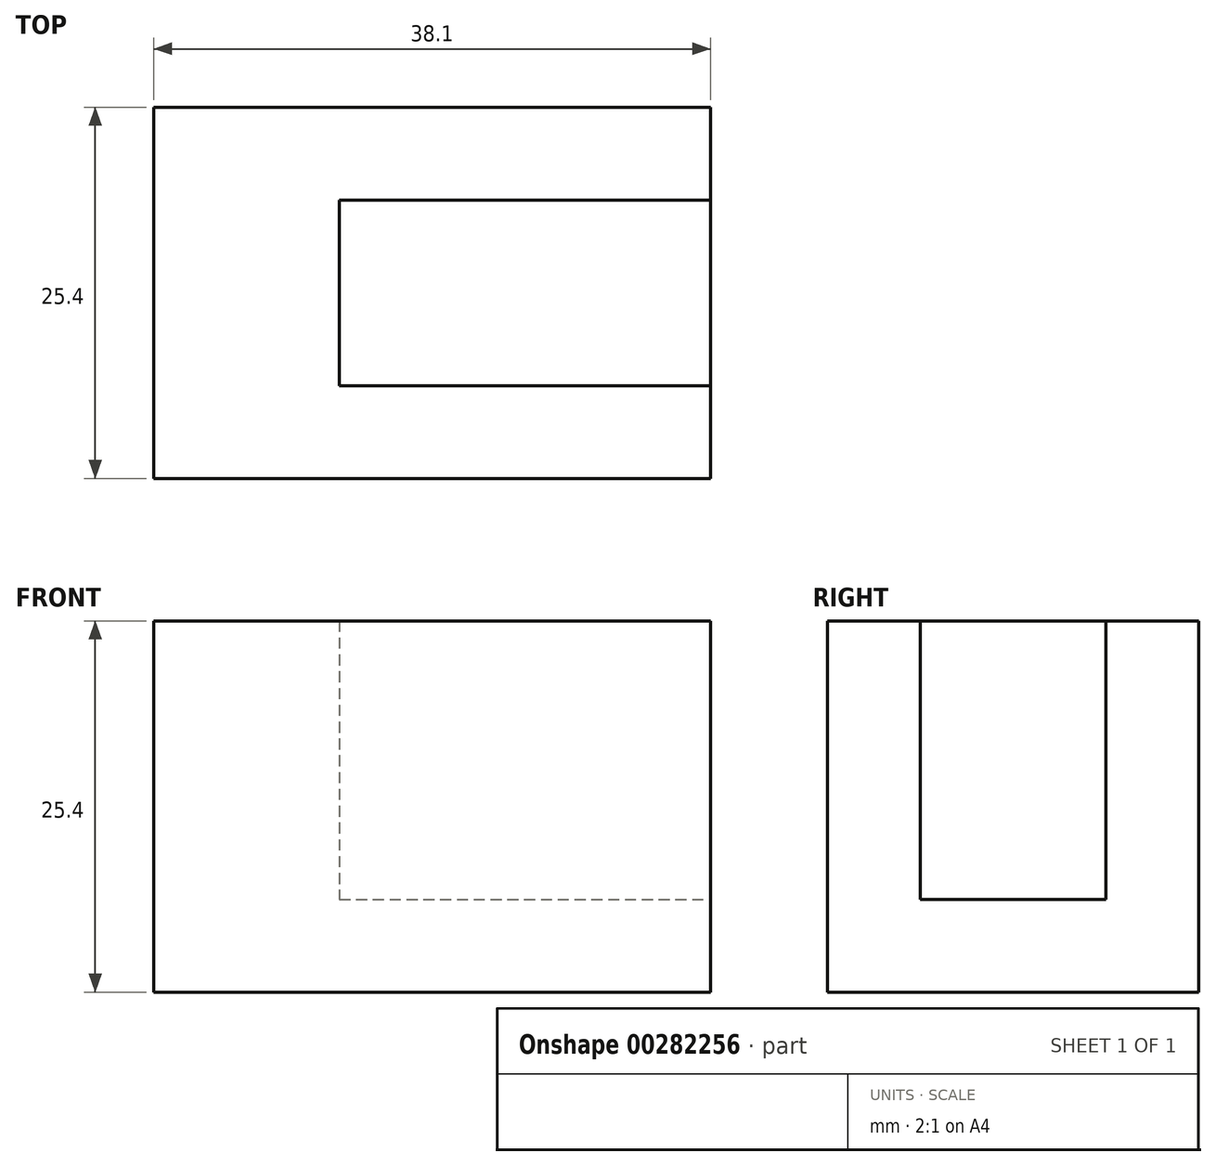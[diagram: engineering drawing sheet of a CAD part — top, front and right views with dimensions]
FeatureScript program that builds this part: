
annotation { "Feature Type Name" : "Feature", "Feature Type Description" : "" }
export const myFeature = defineFeature(function(context is Context, id is Id, definition is map)
    precondition{}
    {
        {
            var Q0;
            Q0=qCreatedBy(makeId("Front.planeOp"),FACE);
            var sketch = newSketch(context, id + "F0", { "sketchPlane" : qUnion([Q0])});
            skLineSegment(sketch, "E0", {"start": v(0, 0) * mm, "end": v(-38.1, 0) * mm});
            skLineSegment(sketch, "E1", {"start": v(-38.1, 0) * mm, "end": v(-38.1, 25.4) * mm});
            skLineSegment(sketch, "E2", {"start": v(-38.1, 25.4) * mm, "end": v(0, 25.4) * mm});
            skLineSegment(sketch, "E3", {"start": v(0, 25.4) * mm, "end": v(0, 0) * mm});
            skSolve(sketch);
        }
        {
            var Q0;
            Q0=makeQuery(id+"F0.imprint","IMPRINT",FACE,{"disambiguationData":[TD([[makeQuery(id+"F0.imprint","IMPRINT",EDGE,{"derivedFrom":sQuery(id+"F0.wireOp",EDGE,"E0")}),-1.0]])]});
            extrude(context, id + "F1", {"entities" : qUnion([Q0]), "depth" : 25.4 * mm});
        }
        {
            var Q0;
            Q0=makeQuery(id+"F1.opExtrude","SWEPT_FACE",FACE,{"disambiguationData":[OSD([sQuery(id+"F0.wireOp",EDGE,"E3")])]});
            var sketch = newSketch(context, id + "F2", { "sketchPlane" : qUnion([Q0])});
            skLineSegment(sketch, "E4", {"start": v(-25.4, 25.4) * mm, "end": v(-19.05, 25.4) * mm});
            skLineSegment(sketch, "E5", {"start": v(-19.05, 25.4) * mm, "end": v(-19.05, 6.35) * mm});
            skLineSegment(sketch, "E6", {"start": v(-19.05, 6.35) * mm, "end": v(-6.35, 6.35) * mm});
            skLineSegment(sketch, "E7", {"start": v(-6.35, 6.35) * mm, "end": v(-6.35, 25.4) * mm});
            skLineSegment(sketch, "E8", {"start": v(-6.35, 25.4) * mm, "end": v(0, 25.4) * mm});
            skSolve(sketch);
        }
        {
            var Q0;
            {var subQ0=sQuery(id+"F2.wireOp",EDGE,"E5");Q0=makeQuery(id+"F2.imprint","IMPRINT",FACE,{"disambiguationData":[TD([[makeQuery(id+"F2.imprint","IMPRINT",EDGE,{"derivedFrom":subQ0}),1.0]])]});}
            extrude(context, id + "F3", {"entities" : qUnion([Q0]), "operationType" : NewBodyOperationType.REMOVE, "oppositeDirection" : true, "depth" : 25.4 * mm});
        }
    });
